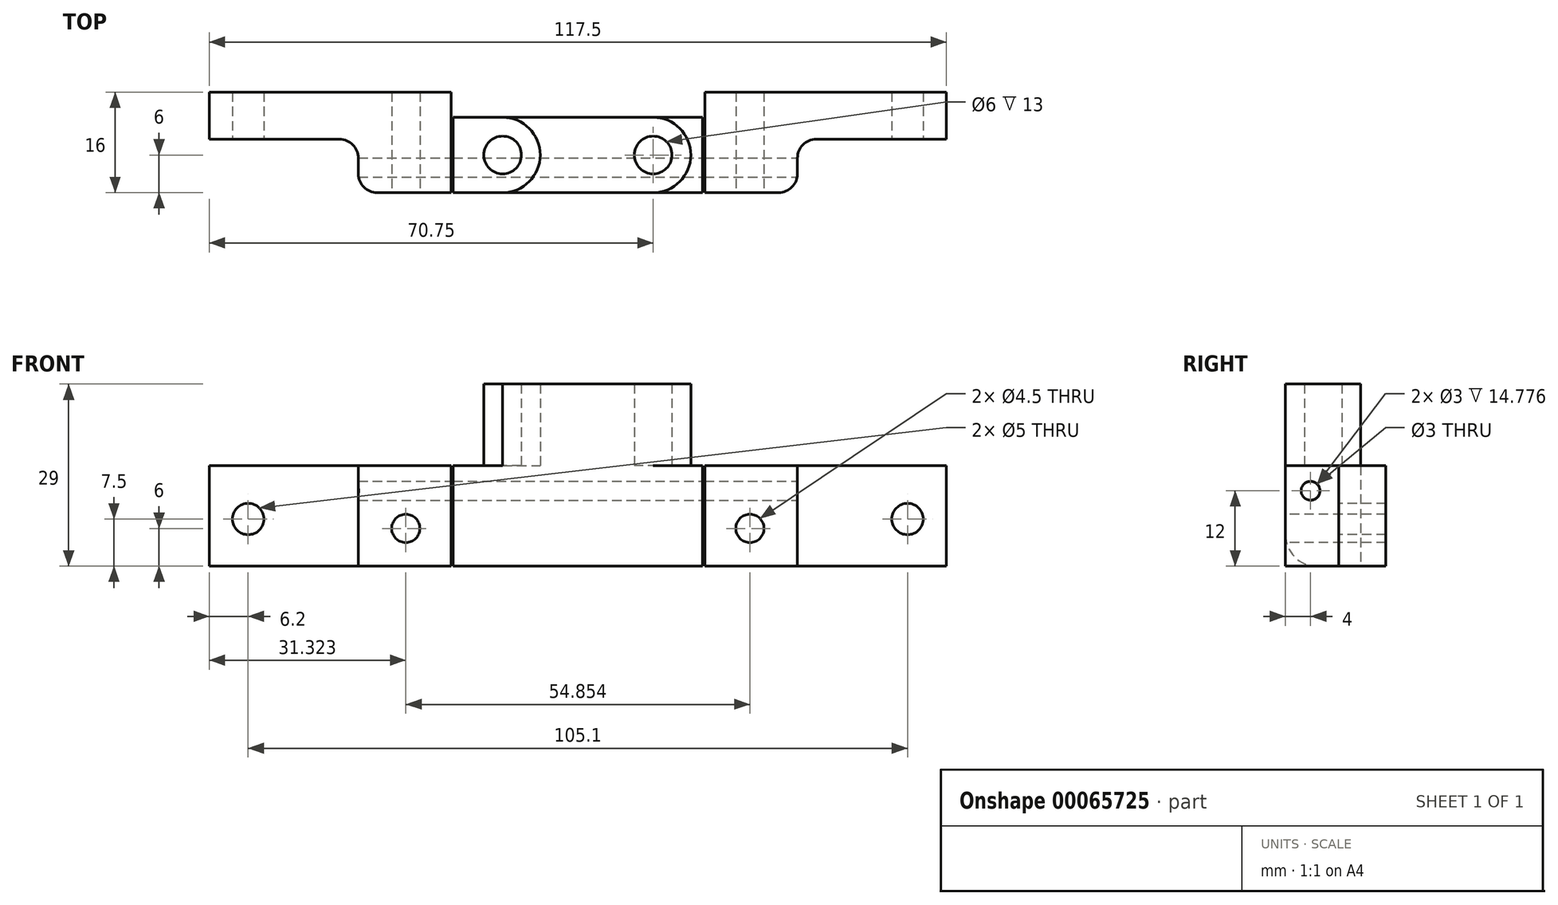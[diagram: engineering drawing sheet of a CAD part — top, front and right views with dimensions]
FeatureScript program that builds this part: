
annotation { "Feature Type Name" : "Feature", "Feature Type Description" : "" }
export const myFeature = defineFeature(function(context is Context, id is Id, definition is map)
    precondition{}
    {
        {
            var Q0;
            Q0=qCreatedBy(makeId("Top.planeOp"),FACE);
            var sketch = newSketch(context, id + "F0", { "sketchPlane" : qUnion([Q0])});
            skPoint(sketch, "E0.rect.middle", {"position": v(0, 0) * mm});
            skLineSegment(sketch, "E1", {"start": v(0, 0) * mm, "end": v(0, 2) * mm});
            skLineSegment(sketch, "E2", {"start": v(0, 2) * mm, "end": v(12, 2) * mm, "construction": true});
            skCircle(sketch, "E3", {"center": v(12, 2) * mm, "radius": 3 * mm});
            skCircle(sketch, "E4", {"center": v(12, 2) * mm, "radius": 6 * mm});
            skCircle(sketch, "E5.MirrorC", {"center": v(-12, 2) * mm, "radius": 3 * mm});
            skCircle(sketch, "E6.MirrorC", {"center": v(-12, 2) * mm, "radius": 6 * mm});
            skLineSegment(sketch, "E7.rect.left", {"start": v(-35, -4) * mm, "end": v(-35, 8) * mm});
            skLineSegment(sketch, "E7.rect.right", {"start": v(35, -4) * mm, "end": v(35, 8) * mm});
            skPoint(sketch, "E7.rect.middle", {"position": v(0, 2) * mm});
            skLineSegment(sketch, "E8", {"start": v(35, -4) * mm, "end": v(20.22, -4) * mm});
            skLineSegment(sketch, "E9", {"start": v(35, 8) * mm, "end": v(-35, 8) * mm});
            skLineSegment(sketch, "E10.rect.top", {"start": v(58.75, 4.5) * mm, "end": v(35, 4.5) * mm});
            skLineSegment(sketch, "E10.rect.left", {"start": v(58.75, 8) * mm, "end": v(58.75, 4.5) * mm});
            skLineSegment(sketch, "E10.rect.right", {"start": v(-58.75, 8) * mm, "end": v(-58.75, 4.5) * mm});
            skPoint(sketch, "E10.rect.middle", {"position": v(0, 8) * mm});
            skLineSegment(sketch, "E11", {"start": v(-58.75, 8) * mm, "end": v(58.75, 8) * mm});
            skPoint(sketch, "E12.orphan", {"position": v(58.75, 11.5) * mm});
            skPoint(sketch, "E13.orphan", {"position": v(-58.75, 11.5) * mm});
            skLineSegment(sketch, "E14.trimOffspring", {"start": v(-35, 4.5) * mm, "end": v(-58.75, 4.5) * mm});
            skLineSegment(sketch, "E15.trimOffspring", {"start": v(17.45, 4.5) * mm, "end": v(13.66, 4.5) * mm});
            skLineSegment(sketch, "E16.left", {"start": v(-19.85, 8) * mm, "end": v(-19.85, -4) * mm});
            skLineSegment(sketch, "E16.right", {"start": v(-20.22, 8) * mm, "end": v(-20.22, -4) * mm});
            skLineSegment(sketch, "E17.MirrorCS", {"start": v(19.85, 8) * mm, "end": v(20.22, 8) * mm});
            skLineSegment(sketch, "E18.MirrorCS", {"start": v(20.22, 8) * mm, "end": v(20.22, -4) * mm});
            skLineSegment(sketch, "E19.MirrorCS", {"start": v(19.85, 8) * mm, "end": v(19.85, -4) * mm});
            skLineSegment(sketch, "E20.trimOffspring", {"start": v(-20.22, -4) * mm, "end": v(-35, -4) * mm});
            skLineSegment(sketch, "E21.trimOffspring", {"start": v(19.85, -4) * mm, "end": v(-19.85, -4) * mm});
            skLineSegment(sketch, "E22", {"start": v(-20.22, 8) * mm, "end": v(-20.22, 12) * mm});
            skLineSegment(sketch, "E23", {"start": v(-20.22, 12) * mm, "end": v(-58.75, 12) * mm});
            skLineSegment(sketch, "E24", {"start": v(-58.75, 12) * mm, "end": v(-58.75, 8) * mm});
            skLineSegment(sketch, "E25", {"start": v(20.22, 12) * mm, "end": v(58.75, 12) * mm});
            skLineSegment(sketch, "E26", {"start": v(58.75, 12) * mm, "end": v(58.75, 8) * mm});
            skLineSegment(sketch, "E27", {"start": v(20.22, 8) * mm, "end": v(20.22, 12) * mm});
            skSolve(sketch);
        }
        {
            var Q0;
            {var subQ4=sQuery(id+"F0.wireOp",EDGE,"E10.rect.right");Q0=makeQuery(id+"F0.imprint","IMPRINT",FACE,{"disambiguationData":[TD([[makeQuery(id+"F0.imprint","IMPRINT",EDGE,{"derivedFrom":subQ4}),1.0]])]});}
            var Q1;
            {var subQ3=sQuery(id+"F0.wireOp",EDGE,"E16.right");Q1=makeQuery(id+"F0.imprint","IMPRINT",FACE,{"disambiguationData":[TD([[makeQuery(id+"F0.imprint","IMPRINT",EDGE,{"derivedFrom":subQ3}),-1.0]])]});}
            var Q2;
            {var subQ5=sQuery(id+"F0.wireOp",EDGE,"E16.left");Q2=makeQuery(id+"F0.imprint","IMPRINT",FACE,{"disambiguationData":[TD([[makeQuery(id+"F0.imprint","IMPRINT",EDGE,{"derivedFrom":subQ5}),1.0]])]});}
            var Q3;
            Q3=makeQuery(id+"F0.imprint","IMPRINT",FACE,{"disambiguationData":[TD([[makeQuery(id+"F0.imprint","IMPRINT",EDGE,{"derivedFrom":sQuery(id+"F0.wireOp",EDGE,"E5.MirrorC")}),1.0]])]});
            var Q4;
            Q4=makeQuery(id+"F0.imprint","IMPRINT",FACE,{"disambiguationData":[TD([[makeQuery(id+"F0.imprint","IMPRINT",EDGE,{"derivedFrom":sQuery(id+"F0.wireOp",EDGE,"E5.MirrorC")}),-1.0]])]});
            var Q5;
            {var subQ0=sQuery(id+"F0.wireOp",EDGE,"E11");var subQ1=sQuery(id+"F0.wireOp",EDGE,"E4");var subQ2=makeQuery(id+"F0.imprint","INTERSECT",VERTEX,{"derivedFrom":[subQ1,subQ0]});Q5=makeQuery(id+"F0.imprint","IMPRINT",FACE,{"disambiguationData":[TD([[makeQuery(id+"F0.imprint","IMPRINT",EDGE,{"disambiguationData":[TD([[subQ2,-1.0]])],"derivedFrom":subQ1}),-1.0]])]});}
            var Q6;
            Q6=makeQuery(id+"F0.imprint","IMPRINT",FACE,{"disambiguationData":[TD([[makeQuery(id+"F0.imprint","IMPRINT",EDGE,{"derivedFrom":sQuery(id+"F0.wireOp",EDGE,"E3")}),-1.0]])]});
            var Q7;
            Q7=makeQuery(id+"F0.imprint","IMPRINT",FACE,{"disambiguationData":[TD([[makeQuery(id+"F0.imprint","IMPRINT",EDGE,{"derivedFrom":sQuery(id+"F0.wireOp",EDGE,"E3")}),1.0]])]});
            var Q8;
            {var subQ0=sQuery(id+"F0.wireOp",EDGE,"E19.MirrorCS");Q8=makeQuery(id+"F0.imprint","IMPRINT",FACE,{"disambiguationData":[TD([[makeQuery(id+"F0.imprint","IMPRINT",EDGE,{"derivedFrom":subQ0}),-1.0]])]});}
            var Q9;
            {var subQ4=sQuery(id+"F0.wireOp",EDGE,"E8");Q9=makeQuery(id+"F0.imprint","IMPRINT",FACE,{"disambiguationData":[TD([[makeQuery(id+"F0.imprint","IMPRINT",EDGE,{"derivedFrom":subQ4}),-1.0]])]});}
            var Q10;
            {var subQ3=sQuery(id+"F0.wireOp",EDGE,"E10.rect.top");Q10=makeQuery(id+"F0.imprint","IMPRINT",FACE,{"disambiguationData":[TD([[makeQuery(id+"F0.imprint","IMPRINT",EDGE,{"derivedFrom":subQ3}),-1.0]])]});}
            var Q11;
            Q11=makeQuery(id+"F0.imprint","IMPRINT",FACE,{"disambiguationData":[TD([[makeQuery(id+"F0.imprint","IMPRINT",EDGE,{"derivedFrom":sQuery(id+"F0.wireOp",EDGE,"E25")}),-1.0]])]});
            var Q12;
            {var subQ0=sQuery(id+"F0.wireOp",EDGE,"E22");Q12=makeQuery(id+"F0.imprint","IMPRINT",FACE,{"disambiguationData":[TD([[makeQuery(id+"F0.imprint","IMPRINT",EDGE,{"derivedFrom":subQ0}),1.0]])]});}
            extrude(context, id + "F1", {"entities" : qUnion([Q0, Q1, Q2, Q3, Q4, Q5, Q6, Q7, Q8, Q9, Q10, Q11, Q12]), "depth" : 16 * mm});
        }
        {
            var Q0;
            Q0=makeQuery(id+"F0.imprint","IMPRINT",FACE,{"disambiguationData":[TD([[makeQuery(id+"F0.imprint","IMPRINT",EDGE,{"derivedFrom":sQuery(id+"F0.wireOp",EDGE,"E5.MirrorC")}),1.0]])]});
            var Q1;
            Q1=makeQuery(id+"F0.imprint","IMPRINT",FACE,{"disambiguationData":[TD([[makeQuery(id+"F0.imprint","IMPRINT",EDGE,{"derivedFrom":sQuery(id+"F0.wireOp",EDGE,"E3")}),-1.0]])]});
            var Q2;
            {var subQ0=sQuery(id+"F0.wireOp",EDGE,"E4");var subQ1=makeQuery(id+"F0.imprint","INTERSECT",VERTEX,{"derivedFrom":[subQ0,sQuery(id+"F0.wireOp",EDGE,"E9")]});Q2=makeQuery(id+"F0.imprint","IMPRINT",FACE,{"disambiguationData":[TD([[makeQuery(id+"F0.imprint","IMPRINT",EDGE,{"disambiguationData":[TD([[subQ1,1.0]])],"derivedFrom":subQ0}),1.0]])]});}
            var Q3;
            {var subQ0=sQuery(id+"F0.wireOp",EDGE,"E6.MirrorC");var subQ1=makeQuery(id+"F0.imprint","INTERSECT",VERTEX,{"derivedFrom":[subQ0,sQuery(id+"F0.wireOp",EDGE,"E9")]});Q3=makeQuery(id+"F0.imprint","IMPRINT",FACE,{"disambiguationData":[TD([[makeQuery(id+"F0.imprint","IMPRINT",EDGE,{"disambiguationData":[TD([[subQ1,1.0]])],"derivedFrom":subQ0}),-1.0]])]});}
            extrude(context, id + "F2", {"entities" : qUnion([Q0, Q1, Q2, Q3]), "operationType" : NewBodyOperationType.ADD, "depth" : 29 * mm});
        }
        {
            var Q0;
            Q0=qCreatedBy(makeId("Front.planeOp"),FACE);
            var sketch = newSketch(context, id + "F3", { "sketchPlane" : qUnion([Q0])});
            skLineSegment(sketch, "E28", {"start": v(0, 0) * mm, "end": v(0, 12) * mm});
            skLineSegment(sketch, "E29", {"start": v(0, 6) * mm, "end": v(-27.43, 6) * mm, "construction": true});
            skCircle(sketch, "E30", {"center": v(-27.43, 6) * mm, "radius": 2.25 * mm});
            skCircle(sketch, "E31.MirrorC", {"center": v(27.43, 6) * mm, "radius": 2.25 * mm});
            skLineSegment(sketch, "E32", {"start": v(0, 6) * mm, "end": v(52.55, 6) * mm, "construction": true});
            skLineSegment(sketch, "E33", {"start": v(0, 0) * mm, "end": v(-52.55, 0) * mm, "construction": true});
            skLineSegment(sketch, "E34", {"start": v(-52.55, 0) * mm, "end": v(-52.55, 5) * mm, "construction": true});
            skLineSegment(sketch, "E35", {"start": v(-52.55, 7.5) * mm, "end": v(-52.55, 5) * mm, "construction": true});
            skCircle(sketch, "E36", {"center": v(-52.55, 7.5) * mm, "radius": 2.5 * mm});
            skCircle(sketch, "E37.MirrorC", {"center": v(52.55, 7.5) * mm, "radius": 2.5 * mm});
            skSolve(sketch);
        }
        {
            var Q0;
            Q0=qSketchRegion(id+"F3",true);
            extrude(context, id + "F4", {"entities" : qUnion([Q0]), "operationType" : NewBodyOperationType.REMOVE, "oppositeDirection" : true, "depth" : 25 * mm, "symmetric" : true});
        }
        {
            var Q0;
            Q0=makeQuery(id+"FM9UNMRZmWFacbX_1.opExtrude","CAP_EDGE",EDGE,{"disambiguationData":[OSD([sQuery(id+"F0.wireOp",EDGE,"E10.rect.right")])],"isStart":false});
            var Q1;
            Q1=makeQuery(id+"F1.opExtrude","SWEPT_EDGE",EDGE,{"disambiguationData":[OSD([sQuery(id+"F0.wireOp",EDGE,"E7.rect.left"),sQuery(id+"F0.wireOp",EDGE,"E20.trimOffspring")])]});
            var Q2;
            Q2=makeQuery(id+"FM9UNMRZmWFacbX_1.opExtrude","CAP_EDGE",EDGE,{"disambiguationData":[OSD([sQuery(id+"F0.wireOp",EDGE,"E10.rect.left")])],"isStart":false});
            var Q3;
            Q3=makeQuery(id+"F1.opExtrude","SWEPT_EDGE",EDGE,{"disambiguationData":[OSD([sQuery(id+"F0.wireOp",EDGE,"E7.rect.right"),sQuery(id+"F0.wireOp",EDGE,"E10.rect.top")])]});
            var Q4;
            Q4=makeQuery(id+"F1.opExtrude","SWEPT_EDGE",EDGE,{"disambiguationData":[OSD([sQuery(id+"F0.wireOp",EDGE,"E7.rect.right"),sQuery(id+"F0.wireOp",EDGE,"E8")])]});
            var Q5;
            Q5=makeQuery(id+"F1.opExtrude","SWEPT_EDGE",EDGE,{"disambiguationData":[OSD([sQuery(id+"F0.wireOp",EDGE,"E7.rect.left"),sQuery(id+"F0.wireOp",EDGE,"E14.trimOffspring")])]});
            fillet(context, id + "F5", {"entities" : qUnion([Q0, Q1, Q2, Q3, Q4, Q5]), "radius" : 3 * mm, "tangentPropagation" : true, "allowEdgeOverflow" : false});
        }
        {
            var Q0;
            Q0=qCreatedBy(makeId("Right.planeOp"),FACE);
            var sketch = newSketch(context, id + "F6", { "sketchPlane" : qUnion([Q0])});
            skLineSegment(sketch, "E38", {"start": v(0, 0) * mm, "end": v(0, 12) * mm});
            skCircle(sketch, "E39", {"center": v(0, 12) * mm, "radius": 1.5 * mm});
            skSolve(sketch);
        }
        {
            var Q0;
            Q0 = qSketchRegion(id + "F6", true);
            extrude(context, id + "F7", {"entities" : qUnion([Q0]), "operationType" : NewBodyOperationType.REMOVE, "oppositeDirection" : true, "depth" : 80 * mm, "symmetric" : true});
        }
        {
            var Q0;
            Q0=makeQuery(id+"F1.opExtrude","CAP_EDGE",EDGE,{"disambiguationData":[OSD([sQuery(id+"F0.wireOp",EDGE,"E21.trimOffspring")])],"isStart":true});
            var Q1;
            {var subQ0=sQuery(id+"F0.wireOp",EDGE,"E11");var subQ1=makeQuery(id+"F0.imprint","INTERSECT",VERTEX,{"derivedFrom":[sQuery(id+"F0.wireOp",EDGE,"E4"),subQ0]});Q1=makeQuery(id+"F1.opExtrude","CAP_EDGE",EDGE,{"disambiguationData":[OSD([subQ0]),TDD([makeQuery(id+"F0.imprint","IMPRINT",EDGE,{"disambiguationData":[TD([[makeQuery(id+"F0.imprint","INTERSECT",VERTEX,{"derivedFrom":[subQ0,sQuery(id+"F0.wireOp",EDGE,"E16.left")]}),-1.0]])],"derivedFrom":subQ0}),makeQuery(id+"F0.imprint","IMPRINT",EDGE,{"disambiguationData":[TD([[subQ1,1.0]])],"derivedFrom":subQ0}),makeQuery(id+"F0.imprint","IMPRINT",EDGE,{"disambiguationData":[TD([[makeQuery(id+"F0.imprint","INTERSECT",VERTEX,{"derivedFrom":[subQ0,sQuery(id+"F0.wireOp",EDGE,"E19.MirrorCS")]}),1.0]])],"derivedFrom":subQ0})])],"isStart":true});}
            fillet(context, id + "F8", {"entities" : qUnion([Q0, Q1]), "radius" : 5 * mm, "tangentPropagation" : true, "allowEdgeOverflow" : false});
        }
    });
